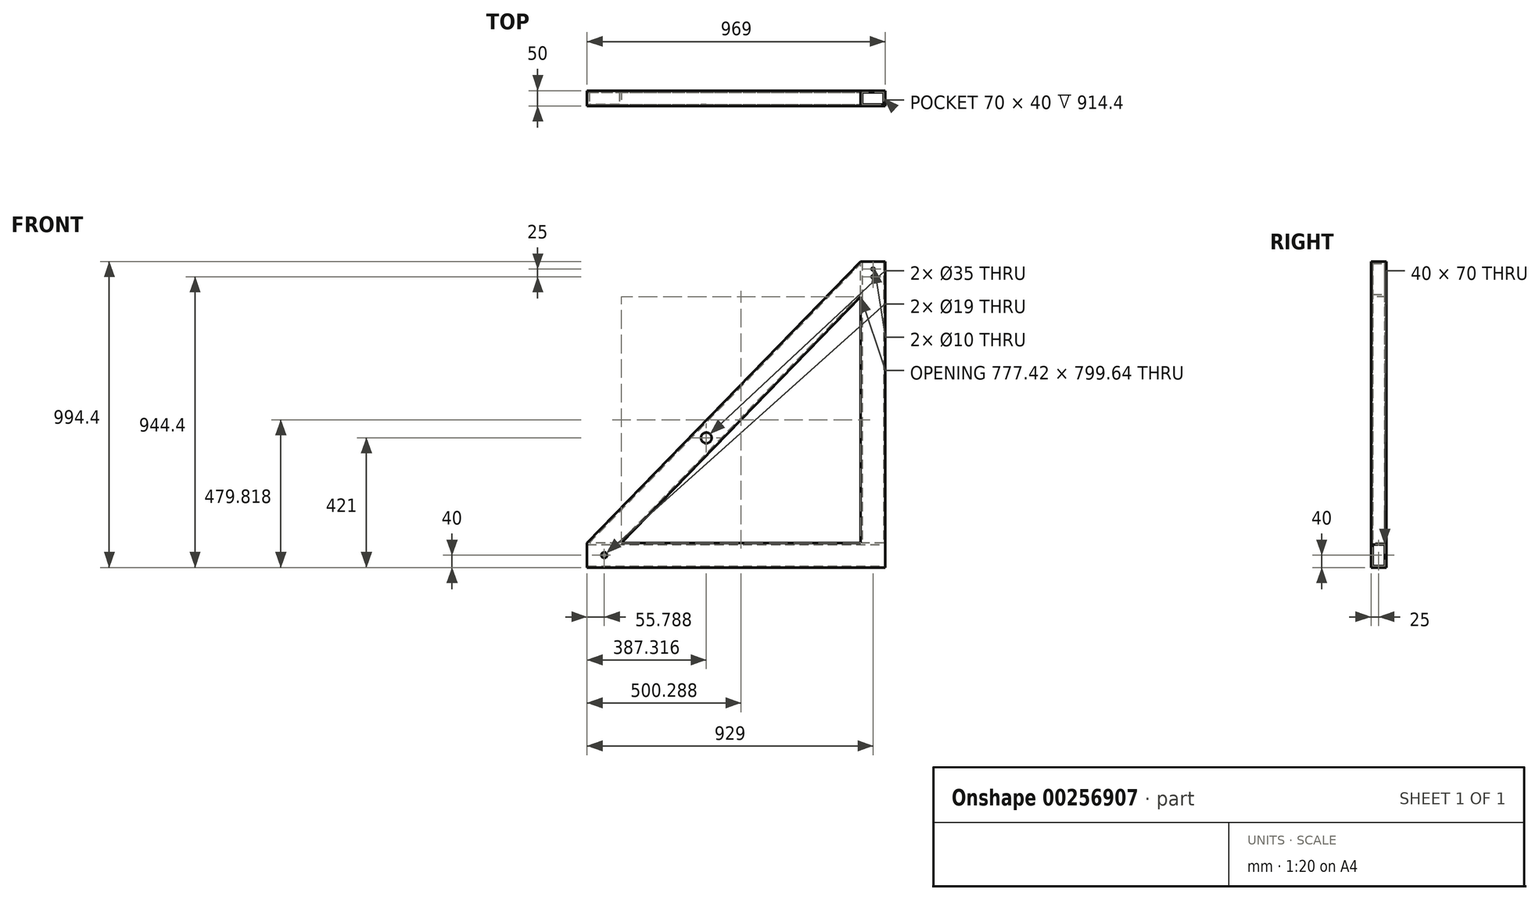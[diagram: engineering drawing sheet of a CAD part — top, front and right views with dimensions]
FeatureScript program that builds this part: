
annotation { "Feature Type Name" : "Feature", "Feature Type Description" : "" }
export const myFeature = defineFeature(function(context is Context, id is Id, definition is map)
    precondition{}
    {
        {
            var Q0;
            Q0=qCreatedBy(makeId("Right.planeOp"),FACE);
            var sketch = newSketch(context, id + "F0", { "sketchPlane" : qUnion([Q0])});
            skLineSegment(sketch, "E0.bottom", {"start": v(0, 0) * mm, "end": v(-50, 0) * mm});
            skLineSegment(sketch, "E0.top", {"start": v(0, 80) * mm, "end": v(-50, 80) * mm});
            skLineSegment(sketch, "E0.left", {"start": v(0, 0) * mm, "end": v(0, 80) * mm});
            skLineSegment(sketch, "E0.right", {"start": v(-50, 0) * mm, "end": v(-50, 80) * mm});
            skLineSegment(sketch, "E1.0", {"start": v(-5, 75) * mm, "end": v(-45, 75) * mm});
            skLineSegment(sketch, "E1.1", {"start": v(-5, 5) * mm, "end": v(-5, 75) * mm});
            skLineSegment(sketch, "E1.2", {"start": v(-5, 5) * mm, "end": v(-45, 5) * mm});
            skLineSegment(sketch, "E1.3", {"start": v(-45, 5) * mm, "end": v(-45, 75) * mm});
            skSolve(sketch);
        }
        {
            var Q0;
            Q0=makeQuery(id+"F0.imprint","IMPRINT",FACE,{"disambiguationData":[TD([[makeQuery(id+"F0.imprint","IMPRINT",EDGE,{"derivedFrom":sQuery(id+"F0.wireOp",EDGE,"E0.bottom")}),-1.0]])]});
            extrude(context, id + "F1", {"entities" : qUnion([Q0]), "oppositeDirection" : true, "depth" : 969 * mm});
        }
        {
            var Q0;
            Q0=makeQuery(id+"F1.opExtrude","SWEPT_FACE",FACE,{"disambiguationData":[OSD([sQuery(id+"F0.wireOp",EDGE,"E0.top")])]});
            var sketch = newSketch(context, id + "F2", { "sketchPlane" : qUnion([Q0])});
            skLineSegment(sketch, "E2.bottom", {"start": v(0, 0) * mm, "end": v(-80, 0) * mm});
            skLineSegment(sketch, "E2.top", {"start": v(0, -50) * mm, "end": v(-80, -50) * mm});
            skLineSegment(sketch, "E2.left", {"start": v(0, 0) * mm, "end": v(0, -50) * mm});
            skLineSegment(sketch, "E2.right", {"start": v(-80, 0) * mm, "end": v(-80, -50) * mm});
            skLineSegment(sketch, "E3.0", {"start": v(-5, -5) * mm, "end": v(-75, -5) * mm});
            skLineSegment(sketch, "E3.1", {"start": v(-5, -5) * mm, "end": v(-5, -45) * mm});
            skLineSegment(sketch, "E3.2", {"start": v(-5, -45) * mm, "end": v(-75, -45) * mm});
            skLineSegment(sketch, "E3.3", {"start": v(-75, -5) * mm, "end": v(-75, -45) * mm});
            skSolve(sketch);
        }
        {
            var Q0;
            Q0=makeQuery(id+"F2.imprint","IMPRINT",FACE,{"disambiguationData":[TD([[makeQuery(id+"F2.imprint","IMPRINT",EDGE,{"derivedFrom":sQuery(id+"F2.wireOp",EDGE,"E2.bottom")}),-1.0]])]});
            extrude(context, id + "F3", {"entities" : qUnion([Q0]), "operationType" : NewBodyOperationType.ADD, "depth" : 914.4 * mm});
        }
        {
            var Q0;
            Q0=makeQuery(id+"F3.boolean.opBoolean","MERGE",FACE,{"derivedFrom":[makeQuery(id+"F1.opExtrude","SWEPT_FACE",FACE,{"disambiguationData":[OSD([sQuery(id+"F0.wireOp",EDGE,"E0.right")])]}),makeQuery(id+"F3.opExtrude","SWEPT_FACE",FACE,{"disambiguationData":[OSD([sQuery(id+"F2.wireOp",EDGE,"E2.top")])]})]});
            var sketch = newSketch(context, id + "F4", { "sketchPlane" : qUnion([Q0])});
            skLineSegment(sketch, "E4", {"start": v(-969, 80) * mm, "end": v(-80, 994.4) * mm});
            skLineSegment(sketch, "E5.0", {"start": v(-857.42, 80) * mm, "end": v(-80, 879.64) * mm});
            skLineSegment(sketch, "E6", {"start": v(-80, 994.4) * mm, "end": v(-80, 879.64) * mm});
            skLineSegment(sketch, "E7", {"start": v(-969, 80) * mm, "end": v(-857.42, 80) * mm});
            skSolve(sketch);
        }
        {
            var Q0;
            Q0=makeQuery(id+"F4.imprint","IMPRINT",FACE,{"disambiguationData":[TD([[makeQuery(id+"F4.imprint","IMPRINT",EDGE,{"derivedFrom":sQuery(id+"F4.wireOp",EDGE,"E4")}),-1.0]])]});
            extrude(context, id + "F5", {"entities" : qUnion([Q0]), "operationType" : NewBodyOperationType.ADD, "oppositeDirection" : true, "depth" : 50 * mm});
        }
        {
            var Q0;
            Q0=makeQuery(id+"F5.boolean.opBoolean","MERGE",FACE,{"derivedFrom":[makeQuery(id+"F3.boolean.opBoolean","MERGE",FACE,{"derivedFrom":[makeQuery(id+"F1.opExtrude","SWEPT_FACE",FACE,{"disambiguationData":[OSD([sQuery(id+"F0.wireOp",EDGE,"E0.right")])]}),makeQuery(id+"F3.opExtrude","SWEPT_FACE",FACE,{"disambiguationData":[OSD([sQuery(id+"F2.wireOp",EDGE,"E2.top")])]})]}),makeQuery(id+"F5.opExtrude","CAP_FACE",FACE,{"disambiguationData":[OSD([sQuery(id+"F4.wireOp",EDGE,"E4"),sQuery(id+"F4.wireOp",EDGE,"E5.0"),sQuery(id+"F4.wireOp",EDGE,"E6"),sQuery(id+"F4.wireOp",EDGE,"E7")])],"isStart":true})]});
            var sketch = newSketch(context, id + "F6", { "sketchPlane" : qUnion([Q0])});
            skCircle(sketch, "E8", {"center": v(-581.68, 421) * mm, "radius": 17.5 * mm});
            skLineSegment(sketch, "E9", {"start": v(-969, 40) * mm, "end": v(0, 40) * mm, "construction": true});
            skLineSegment(sketch, "E10", {"start": v(-40, 994.4) * mm, "end": v(-40, 0) * mm, "construction": true});
            skLineSegment(sketch, "E11.0", {"start": v(-952.1, 40) * mm, "end": v(-40, 978.16) * mm, "construction": true});
            skPoint(sketch, "E12", {"position": v(-40, 40) * mm});
            skLineSegment(sketch, "E13", {"start": v(-969, 80) * mm, "end": v(-857.42, 80) * mm, "construction": true});
            skCircle(sketch, "E14", {"center": v(-913.21, 40) * mm, "radius": 9.5 * mm});
            skPoint(sketch, "E14.centerSnap0", {"position": v(-913.21, 80) * mm});
            skCircle(sketch, "E15", {"center": v(-40, 969.4) * mm, "radius": 5 * mm});
            skCircle(sketch, "E16", {"center": v(-40, 944.4) * mm, "radius": 5 * mm});
            skLineSegment(sketch, "E17.bottom", {"start": v(0, 994.4) * mm, "end": v(-80, 994.4) * mm});
            skLineSegment(sketch, "E17.top", {"start": v(0, 914.4) * mm, "end": v(-80, 914.4) * mm});
            skLineSegment(sketch, "E17.left", {"start": v(0, 994.4) * mm, "end": v(0, 914.4) * mm});
            skLineSegment(sketch, "E17.right", {"start": v(-80, 994.4) * mm, "end": v(-80, 914.4) * mm});
            skCircle(sketch, "E18", {"center": v(-40, 895.35) * mm, "radius": 19.05 * mm});
            skPoint(sketch, "E19", {"position": v(-40, 622.3) * mm});
            skCircle(sketch, "E20", {"center": v(-913.21, 40) * mm, "radius": 127 * mm, "construction": true});
            skLineSegment(sketch, "E21", {"start": v(-913.21, -87) * mm, "end": v(120.6, -87) * mm, "construction": true});
            skLineSegment(sketch, "E22", {"start": v(-87.13, -87) * mm, "end": v(-87.13, 55.88) * mm, "construction": true});
            skLineSegment(sketch, "E23", {"start": v(-40, 969.4) * mm, "end": v(-40, 1071) * mm, "construction": true});
            skSolve(sketch);
        }
        {
            var Q0;
            Q0=makeQuery(id+"F6.imprint","IMPRINT",FACE,{"disambiguationData":[TD([[makeQuery(id+"F6.imprint","IMPRINT",EDGE,{"derivedFrom":sQuery(id+"F6.wireOp",EDGE,"E8")}),1.0]])]});
            var Q1;
            Q1=makeQuery(id+"F6.imprint","IMPRINT",FACE,{"disambiguationData":[TD([[makeQuery(id+"F6.imprint","IMPRINT",EDGE,{"derivedFrom":sQuery(id+"F6.wireOp",EDGE,"E14")}),1.0]])]});
            var Q2;
            Q2=makeQuery(id+"F6.imprint","IMPRINT",FACE,{"disambiguationData":[TD([[makeQuery(id+"F6.imprint","IMPRINT",EDGE,{"derivedFrom":sQuery(id+"F6.wireOp",EDGE,"0ojQ3yUH-WDDA-yJU1-obOh-HxR2YhjMYrnh")}),1.0]])]});
            var Q3;
            Q3=makeQuery(id+"F6.imprint","IMPRINT",FACE,{"disambiguationData":[TD([[makeQuery(id+"F6.imprint","IMPRINT",EDGE,{"derivedFrom":sQuery(id+"F6.wireOp",EDGE,"d8IdI36S-K7sh-dgoY-yQy2-2eaBgbG5GFEp")}),1.0]])]});
            extrude(context, id + "F7", {"entities" : qUnion([Q0, Q1, Q2, Q3]), "operationType" : NewBodyOperationType.REMOVE, "endBound" : BoundingType.THROUGH_ALL, "oppositeDirection" : true, "depth" : 25.4 * mm});
        }
        {
            var Q0;
            Q0=makeQuery(id+"F7.boolean.opBoolean","COPY",FACE,{"derivedFrom":makeQuery(id+"F7.opExtrude","SWEPT_FACE",FACE,{"disambiguationData":[OSD([sQuery(id+"F6.wireOp",EDGE,"E8")])]})});
            var Q1;
            Q1=makeQuery(id+"F1.opExtrude","SWEPT_BODY",BODY,{"disambiguationData":[OSD([sQuery(id+"F0.wireOp",EDGE,"E0.bottom"),sQuery(id+"F0.wireOp",EDGE,"E0.top"),sQuery(id+"F0.wireOp",EDGE,"E0.left"),sQuery(id+"F0.wireOp",EDGE,"E0.right"),sQuery(id+"F0.wireOp",EDGE,"E1.0"),sQuery(id+"F0.wireOp",EDGE,"E1.1"),sQuery(id+"F0.wireOp",EDGE,"E1.2"),sQuery(id+"F0.wireOp",EDGE,"E1.3")])]});
            shell(context, id + "F8", {"entities" : qUnion([Q0]), "parts" : qUnion([Q1]), "thickness" : 5 * mm});
        }
        {
            var Q0;
            Q0=makeQuery(id+"F6.imprint","IMPRINT",FACE,{"disambiguationData":[TD([[makeQuery(id+"F6.imprint","IMPRINT",EDGE,{"derivedFrom":sQuery(id+"F6.wireOp",EDGE,"E15")}),1.0]])]});
            var Q1;
            Q1=makeQuery(id+"F6.imprint","IMPRINT",FACE,{"disambiguationData":[TD([[makeQuery(id+"F6.imprint","IMPRINT",EDGE,{"derivedFrom":sQuery(id+"F6.wireOp",EDGE,"E16")}),1.0]])]});
            extrude(context, id + "F9", {"entities" : qUnion([Q0, Q1]), "operationType" : NewBodyOperationType.REMOVE, "endBound" : BoundingType.UP_TO_NEXT, "oppositeDirection" : true, "depth" : 25.4 * mm});
        }
    });
